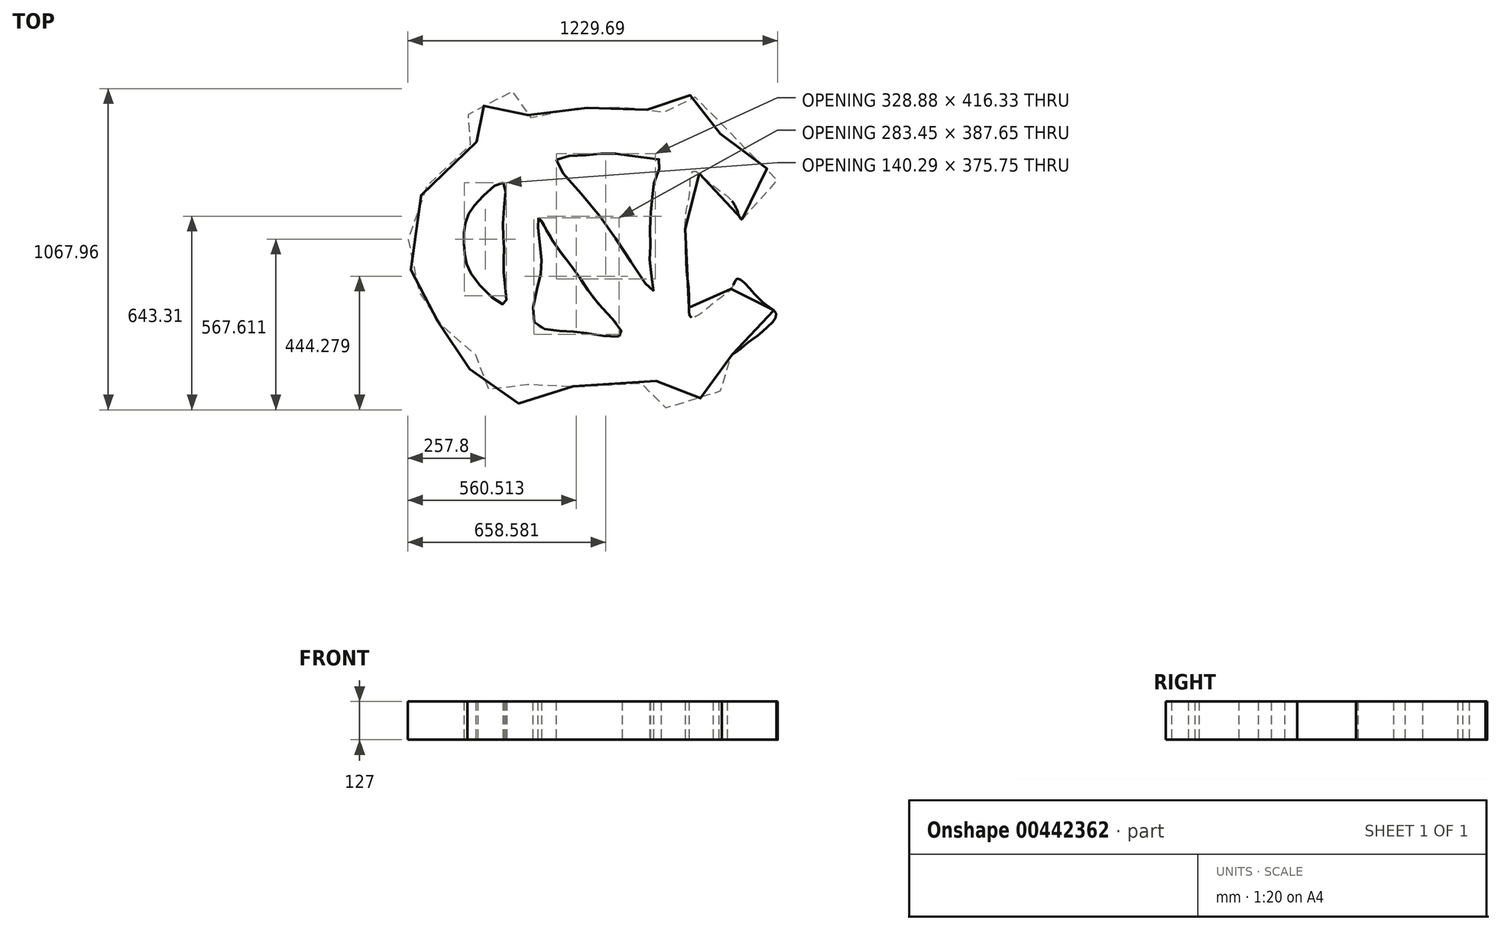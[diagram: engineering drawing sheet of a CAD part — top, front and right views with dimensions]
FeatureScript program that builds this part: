
annotation { "Feature Type Name" : "Feature", "Feature Type Description" : "" }
export const myFeature = defineFeature(function(context is Context, id is Id, definition is map)
    precondition{}
    {
        {
            var Q0;
            Q0=qCreatedBy(makeId("Top.planeOp"),FACE);
            var sketch = newSketch(context, id + "F0", { "sketchPlane" : qUnion([Q0])});
            skFitSpline(sketch, "E0", {"points": [v(496, 98.2) * mm, v(559.03, 162.85) * mm, v(613.99, 222.65) * mm, v(583.28, 263.06) * mm, v(541.26, 308.31) * mm, v(487.92, 348.72) * mm, v(449.13, 372.96) * mm, v(420.04, 387.5) * mm, v(434.58, 437.61) * mm, v(445.9, 465.09) * mm, v(405.49, 479.64) * mm, v(261.64, 528.12) * mm, v(253.56, 505.5) * mm, v(237.4, 455.4) * mm, v(188.91, 460.24) * mm, v(145.27, 468.32) * mm, v(83.85, 471.55) * mm, v(41.83, 473.17) * mm, v(-34.13, 468.32) * mm, v(-90.7, 465.09) * mm, v(-155.35, 450.54) * mm, v(-208.69, 437.61) * mm, v(-228.08, 499.03) * mm, v(-238.8, 532.77) * mm, v(-290.63, 511.18) * mm, v(-400.76, 461.51) * mm, v(-416.4, 453.7) * mm, v(-405.65, 426.34) * mm, v(-388.06, 373.6) * mm, v(-383.18, 360.9) * mm, v(-423.23, 338.42) * mm, v(-500.4, 271.02) * mm, v(-567.81, 185.05) * mm, v(-601.02, 99.08) * mm, v(-615.68, 8.23) * mm, v(-602, -82.62) * mm, v(-573.68, -150.07) * mm, v(-543.45, -191.37) * mm, v(-527.93, -223.14) * mm, v(-495.27, -263.06) * mm, v(-440.85, -310.23) * mm, v(-390.05, -335.62) * mm, v(-417.26, -424.52) * mm, v(-395.5, -444.48) * mm, v(-328.37, -477.13) * mm, v(-248.54, -513.41) * mm, v(-217.7, -444.48) * mm, v(-208.63, -424.52) * mm, v(-101.6, -449.92) * mm, v(39.91, -458.99) * mm, v(148.76, -448.1) * mm, v(215.89, -440.85) * mm, v(226.77, -484.39) * mm, v(250.36, -533.37) * mm, v(335.62, -502.53) * mm, v(428.15, -462.62) * mm, v(399.12, -388.24) * mm, v(449.92, -357.4) * mm, v(502.53, -321.11) * mm, v(556.96, -279.38) * mm, v(609.57, -217.7) * mm, v(582.35, -190.49) * mm, v(537, -148.76) * mm, v(480.76, -97.97) * mm, v(462.62, -127) * mm, v(417.26, -166.9) * mm, v(371.9, -203.19) * mm, v(326.55, -226.77) * mm, v(319.3, -159.65) * mm, v(312.04, -78.01) * mm, v(308.41, 30.84) * mm, v(308.41, 116.1) * mm, v(321.11, 185.05) * mm, v(332, 259.43) * mm, v(380.98, 226.77) * mm, v(439.03, 181.42) * mm, v(475.32, 137.88) * mm, v(496, 98.2) * mm]});
            skFitSpline(sketch, "E1", {"points": [v(-121.55, 297.53) * mm, v(-52.61, 310.23) * mm, v(25.4, 317.48) * mm, v(96.15, 315.67) * mm, v(161.46, 304.78) * mm, v(224.96, 293.9) * mm, v(208.63, 239.47) * mm, v(197.75, 174.16) * mm, v(190.49, 94.34) * mm, v(190.49, 0) * mm, v(190.49, -63.5) * mm, v(199.56, -139.7) * mm, v(125.18, -39.91) * mm, v(-27.21, 170.53) * mm, v(-121.55, 297.53) * mm]});
            skFitSpline(sketch, "E2", {"points": [v(-181.42, 103.67) * mm, v(-174.16, 0) * mm, v(-177.8, -101.75) * mm, v(-194.12, -244.92) * mm, v(-101.6, -272.13) * mm, v(0, -283.01) * mm, v(96.15, -284.83) * mm, v(18.14, -181.42) * mm, v(-56.24, -78.01) * mm, v(-141.5, 39.91) * mm, v(-181.42, 103.67) * mm]});
            skFitSpline(sketch, "E3", {"points": [v(-298.47, 221.06) * mm, v(-298.92, 103.67) * mm, v(-295.87, 0) * mm, v(-294.66, -101.75) * mm, v(-293.7, -183.3) * mm, v(-391.4, -101.75) * mm, v(-424.1, -32.7) * mm, v(-429.22, 39.88) * mm, v(-419.53, 103.67) * mm, v(-376.82, 164.3) * mm, v(-298.47, 221.06) * mm]});
            skSolve(sketch);
        }
        {
            var Q0;
            Q0=makeQuery(id+"F0.imprint","IMPRINT",FACE,{"disambiguationData":[TD([[makeQuery(id+"F0.imprint","IMPRINT",EDGE,{"derivedFrom":sQuery(id+"F0.wireOp",EDGE,"E0")}),1.0]])]});
            extrude(context, id + "F1", {"entities" : qUnion([Q0]), "depth" : 127 * mm});
        }
    });
